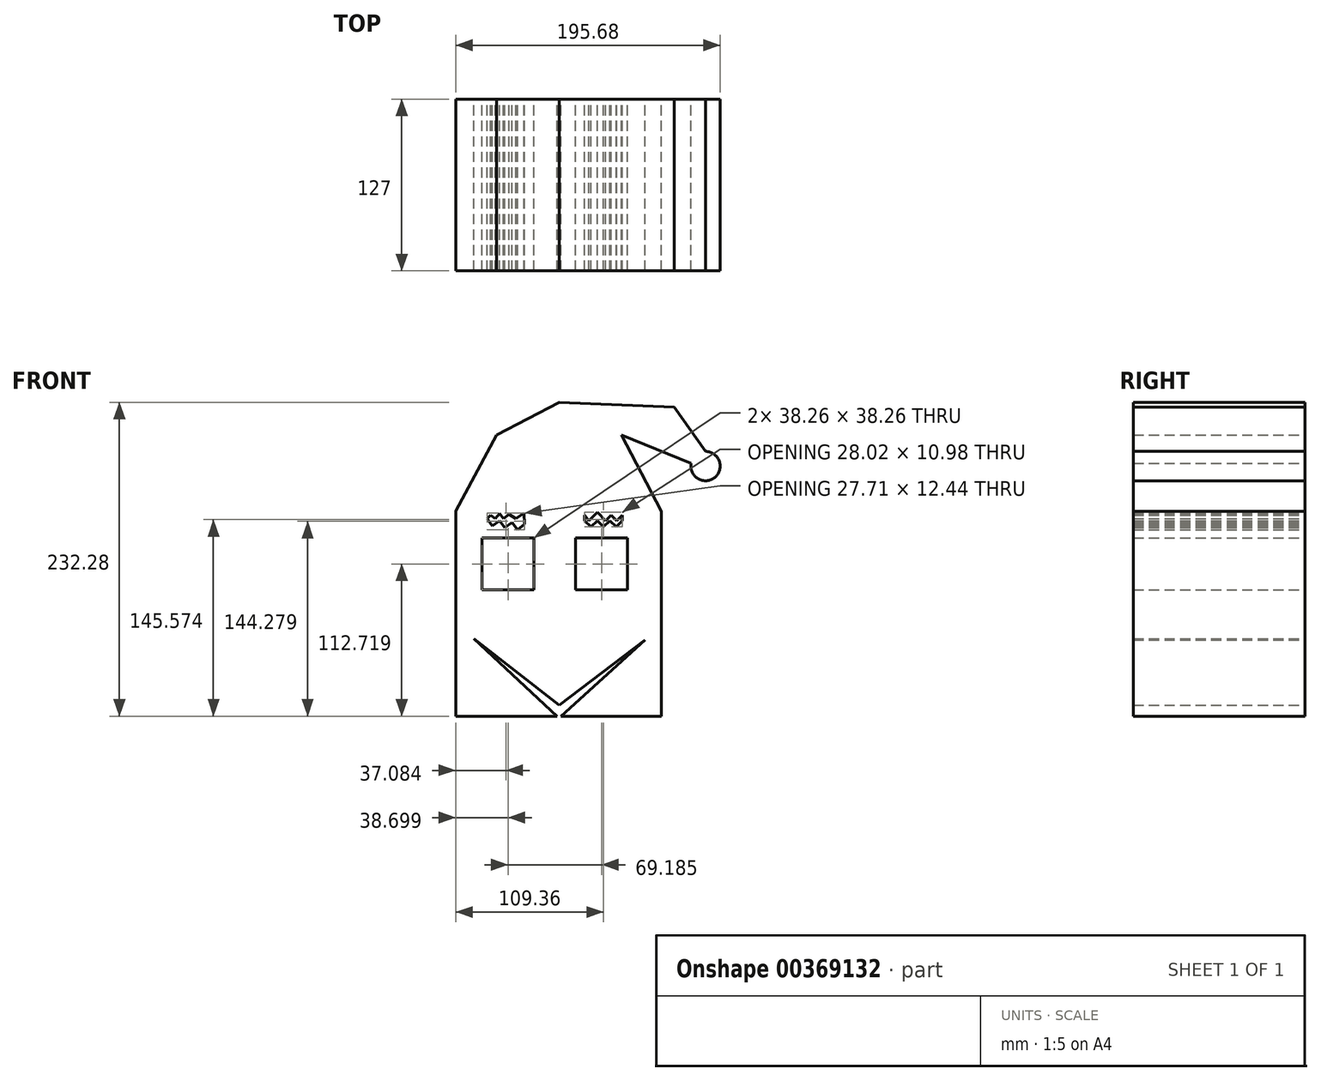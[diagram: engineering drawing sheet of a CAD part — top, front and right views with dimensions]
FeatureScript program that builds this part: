
annotation { "Feature Type Name" : "Feature", "Feature Type Description" : "" }
export const myFeature = defineFeature(function(context is Context, id is Id, definition is map)
    precondition{}
    {
        {
            var Q0;
            Q0=qCreatedBy(makeId("Front.planeOp"),FACE);
            var sketch = newSketch(context, id + "F0", { "sketchPlane" : qUnion([Q0])});
            skLineSegment(sketch, "E0", {"start": v(-63.03, -18.42) * mm, "end": v(0, -67.63) * mm});
            skLineSegment(sketch, "E1", {"start": v(0, -67.63) * mm, "end": v(63.68, -19.26) * mm});
            skLineSegment(sketch, "E2", {"start": v(-56.88, 56.1) * mm, "end": v(-56.88, 17.84) * mm});
            skLineSegment(sketch, "E3", {"start": v(-56.88, 17.84) * mm, "end": v(-18.62, 17.84) * mm});
            skLineSegment(sketch, "E4", {"start": v(-18.62, 17.84) * mm, "end": v(-18.62, 56.1) * mm});
            skLineSegment(sketch, "E5", {"start": v(-18.62, 56.1) * mm, "end": v(-56.88, 56.1) * mm});
            skLineSegment(sketch, "E6", {"start": v(12.3, 56.1) * mm, "end": v(12.3, 17.84) * mm});
            skLineSegment(sketch, "E7", {"start": v(12.3, 17.84) * mm, "end": v(50.56, 17.84) * mm});
            skLineSegment(sketch, "E8", {"start": v(50.56, 17.84) * mm, "end": v(50.56, 56.1) * mm});
            skLineSegment(sketch, "E9", {"start": v(50.56, 56.1) * mm, "end": v(12.3, 56.1) * mm});
            skLineSegment(sketch, "E10", {"start": v(-53.22, 70.39) * mm, "end": v(-49.3, 65.08) * mm});
            skLineSegment(sketch, "E11", {"start": v(-49.3, 65.08) * mm, "end": v(-43.98, 69) * mm});
            skLineSegment(sketch, "E12", {"start": v(-43.98, 69) * mm, "end": v(-40.06, 63.7) * mm});
            skLineSegment(sketch, "E13", {"start": v(-40.06, 63.7) * mm, "end": v(-34.75, 67.62) * mm});
            skLineSegment(sketch, "E14", {"start": v(-34.75, 67.62) * mm, "end": v(-30.82, 62.3) * mm});
            skLineSegment(sketch, "E15", {"start": v(-30.82, 62.3) * mm, "end": v(-25.51, 66.23) * mm});
            skLineSegment(sketch, "E16", {"start": v(18.9, 69) * mm, "end": v(23.57, 64.33) * mm});
            skLineSegment(sketch, "E17", {"start": v(23.57, 64.33) * mm, "end": v(28.24, 69) * mm});
            skLineSegment(sketch, "E18", {"start": v(28.24, 69) * mm, "end": v(32.9, 64.33) * mm});
            skLineSegment(sketch, "E19", {"start": v(32.9, 64.33) * mm, "end": v(37.58, 69) * mm});
            skLineSegment(sketch, "E20", {"start": v(37.58, 69) * mm, "end": v(42.25, 64.33) * mm});
            skLineSegment(sketch, "E21", {"start": v(42.25, 64.33) * mm, "end": v(46.92, 69) * mm});
            skLineSegment(sketch, "E22", {"start": v(-50.65, 73.1) * mm, "end": v(-47.2, 70.39) * mm});
            skLineSegment(sketch, "E23", {"start": v(-47.2, 70.39) * mm, "end": v(-44.12, 74.3) * mm});
            skLineSegment(sketch, "E24", {"start": v(-44.12, 74.3) * mm, "end": v(-41.23, 70.39) * mm});
            skLineSegment(sketch, "E25", {"start": v(-41.23, 70.39) * mm, "end": v(-36.9, 73.58) * mm});
            skLineSegment(sketch, "E26", {"start": v(-36.9, 73.58) * mm, "end": v(-31.95, 70.39) * mm});
            skLineSegment(sketch, "E27", {"start": v(-31.95, 70.39) * mm, "end": v(-26.04, 74.75) * mm});
            skLineSegment(sketch, "E28", {"start": v(-26.04, 74.75) * mm, "end": v(-25.51, 66.23) * mm});
            skLineSegment(sketch, "E29", {"start": v(-53.22, 70.39) * mm, "end": v(-50.65, 73.1) * mm});
            skLineSegment(sketch, "E30", {"start": v(18.9, 73.1) * mm, "end": v(21.93, 69) * mm});
            skLineSegment(sketch, "E31", {"start": v(21.93, 69) * mm, "end": v(28.24, 75.31) * mm});
            skLineSegment(sketch, "E32", {"start": v(28.24, 75.31) * mm, "end": v(34.55, 69) * mm});
            skLineSegment(sketch, "E33", {"start": v(34.55, 69) * mm, "end": v(38.65, 73.1) * mm});
            skLineSegment(sketch, "E34", {"start": v(38.65, 73.1) * mm, "end": v(42.75, 69) * mm});
            skLineSegment(sketch, "E35", {"start": v(42.75, 69) * mm, "end": v(46.85, 73.1) * mm});
            skLineSegment(sketch, "E36", {"start": v(46.85, 73.1) * mm, "end": v(46.92, 69) * mm});
            skLineSegment(sketch, "E37", {"start": v(18.9, 73.1) * mm, "end": v(18.9, 69) * mm});
            skLineSegment(sketch, "E38", {"start": v(-63.03, -18.42) * mm, "end": v(0, -77.13) * mm});
            skLineSegment(sketch, "E39", {"start": v(0, -77.13) * mm, "end": v(63.68, -19.26) * mm});
            skLineSegment(sketch, "E40", {"start": v(-76.45, 76.27) * mm, "end": v(-76.45, -75.75) * mm});
            skLineSegment(sketch, "E41", {"start": v(-76.45, -75.75) * mm, "end": v(75.7, -75.75) * mm});
            skLineSegment(sketch, "E42", {"start": v(75.7, -75.75) * mm, "end": v(75.7, 76.04) * mm});
            skLineSegment(sketch, "E43", {"start": v(75.7, 76.04) * mm, "end": v(-76.45, 76.27) * mm});
            skLineSegment(sketch, "E44", {"start": v(-76.45, 76.27) * mm, "end": v(-46.07, 132.36) * mm});
            skLineSegment(sketch, "E45", {"start": v(-46.07, 132.36) * mm, "end": v(0, 156.53) * mm});
            skLineSegment(sketch, "E46", {"start": v(0, 156.53) * mm, "end": v(46.19, 132.58) * mm});
            skLineSegment(sketch, "E47", {"start": v(46.19, 132.58) * mm, "end": v(75.7, 76.04) * mm});
            skLineSegment(sketch, "E48", {"start": v(46.19, 132.58) * mm, "end": v(85.28, 152.99) * mm});
            skLineSegment(sketch, "E49", {"start": v(85.28, 152.99) * mm, "end": v(0, 156.53) * mm});
            skLineSegment(sketch, "E50", {"start": v(46.19, 132.58) * mm, "end": v(97.73, 111.46) * mm});
            skLineSegment(sketch, "E51", {"start": v(97.73, 111.46) * mm, "end": v(85.28, 152.99) * mm});
            skLineSegment(sketch, "E52", {"start": v(85.28, 152.99) * mm, "end": v(108.6, 119.86) * mm});
            skLineSegment(sketch, "E53", {"start": v(108.6, 119.86) * mm, "end": v(97.73, 111.46) * mm});
            skArc(sketch, "E54", {"start": v(97.73, 111.46) * mm, "mid": v(115.32, 101.07) * mm, "end": v(108.3, 120.26) * mm});
            skSolve(sketch);
        }
        {
            var Q0;
            {var subQ1=sQuery(id+"F0.wireOp",EDGE,"E0");Q0=makeQuery(id+"F0.imprint","IMPRINT",FACE,{"disambiguationData":[TD([[makeQuery(id+"F0.imprint","IMPRINT",EDGE,{"derivedFrom":subQ1}),1.0]])]});}
            var Q1;
            Q1=makeQuery(id+"F0.imprint","IMPRINT",FACE,{"disambiguationData":[TD([[makeQuery(id+"F0.imprint","IMPRINT",EDGE,{"derivedFrom":sQuery(id+"F0.wireOp",EDGE,"E43")}),-1.0]])]});
            var Q2;
            Q2=makeQuery(id+"F0.imprint","IMPRINT",FACE,{"disambiguationData":[TD([[makeQuery(id+"F0.imprint","IMPRINT",EDGE,{"derivedFrom":sQuery(id+"F0.wireOp",EDGE,"E46")}),1.0]])]});
            var Q3;
            Q3=makeQuery(id+"F0.imprint","IMPRINT",FACE,{"disambiguationData":[TD([[makeQuery(id+"F0.imprint","IMPRINT",EDGE,{"derivedFrom":sQuery(id+"F0.wireOp",EDGE,"E48")}),-1.0]])]});
            var Q4;
            {var subQ0=sQuery(id+"F0.wireOp",EDGE,"E51");Q4=makeQuery(id+"F0.imprint","IMPRINT",FACE,{"disambiguationData":[TD([[makeQuery(id+"F0.imprint","IMPRINT",EDGE,{"derivedFrom":subQ0}),-1.0]])]});}
            var Q5;
            {var subQ0=sQuery(id+"F0.wireOp",EDGE,"E53");Q5=makeQuery(id+"F0.imprint","IMPRINT",FACE,{"disambiguationData":[TD([[makeQuery(id+"F0.imprint","IMPRINT",EDGE,{"derivedFrom":subQ0}),1.0]])]});}
            extrude(context, id + "F1", {"entities" : qUnion([Q0, Q1, Q2, Q3, Q4, Q5]), "depth" : 127 * mm});
        }
    });
